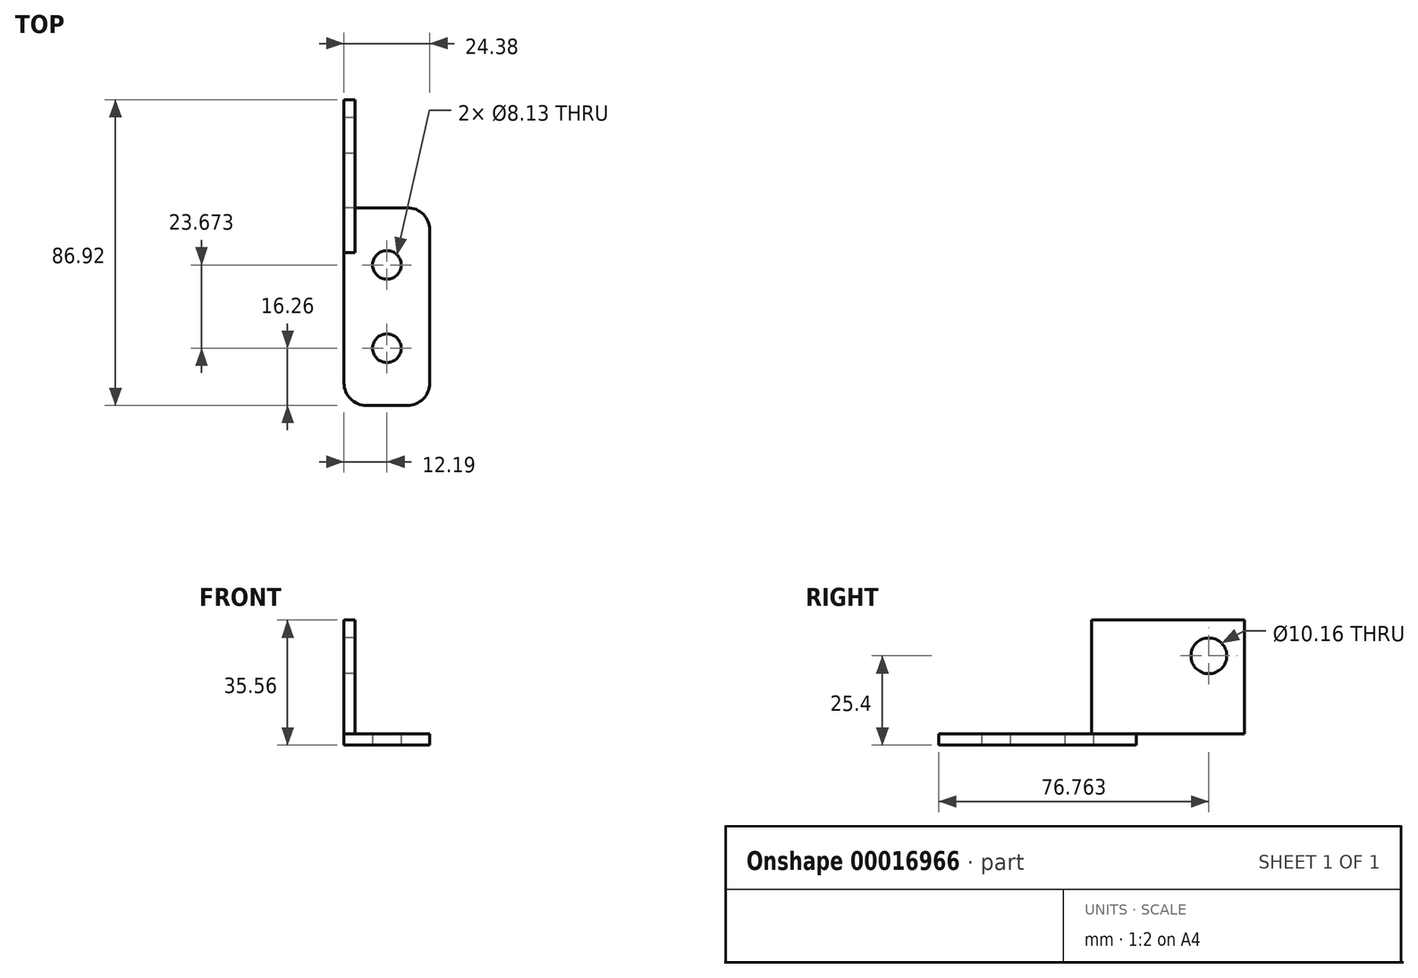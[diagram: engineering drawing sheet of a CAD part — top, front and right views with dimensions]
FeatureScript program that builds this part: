
annotation { "Feature Type Name" : "Feature", "Feature Type Description" : "" }
export const myFeature = defineFeature(function(context is Context, id is Id, definition is map)
    precondition{}
    {
        {
            var Q0;
            Q0=qCreatedBy(makeId("Top.planeOp"),FACE);
            var sketch = newSketch(context, id + "F0", { "sketchPlane" : qUnion([Q0])});
            skCircle(sketch, "E0", {"center": v(0, 0) * mm, "radius": 4.06 * mm});
            skCircle(sketch, "E1", {"center": v(0, 23.67) * mm, "radius": 4.06 * mm});
            skLineSegment(sketch, "E2", {"start": v(0, 19.6) * mm, "end": v(0, 4.06) * mm, "construction": true});
            skLineSegment(sketch, "E3.rect.bottom", {"start": v(5.84, -16.26) * mm, "end": v(-5.84, -16.26) * mm});
            skLineSegment(sketch, "E3.rect.top", {"start": v(5.84, 39.93) * mm, "end": v(-12.2, 39.93) * mm});
            skLineSegment(sketch, "E3.rect.left", {"start": v(12.2, -9.9) * mm, "end": v(12.2, 33.58) * mm});
            skLineSegment(sketch, "E3.rect.right", {"start": v(-12.2, -9.9) * mm, "end": v(-12.2, 39.93) * mm});
            skPoint(sketch, "E3.rect.middle", {"position": v(0, 11.84) * mm});
            skLineSegment(sketch, "E4", {"start": v(0, 11.84) * mm, "end": v(12.2, 11.84) * mm, "construction": true});
            skLineSegment(sketch, "E5", {"start": v(0, 39.93) * mm, "end": v(0, 27.74) * mm, "construction": true});
            skPoint(sketch, "E6.visualSharp", {"position": v(12.2, -16.26) * mm});
            skArc(sketch, "E6.filletArc", {"start": v(5.84, -16.26) * mm, "mid": v(10.33, -14.4) * mm, "end": v(12.2, -9.9) * mm});
            skPoint(sketch, "E7.visualSharp", {"position": v(-12.2, -16.26) * mm});
            skArc(sketch, "E7.filletArc", {"start": v(-12.2, -9.9) * mm, "mid": v(-10.33, -14.4) * mm, "end": v(-5.84, -16.26) * mm});
            skPoint(sketch, "E8.visualSharp", {"position": v(12.2, 39.93) * mm});
            skArc(sketch, "E8.filletArc", {"start": v(12.2, 33.58) * mm, "mid": v(10.33, 38.07) * mm, "end": v(5.84, 39.93) * mm});
            skSolve(sketch);
        }
        {
            var Q0;
            Q0=makeQuery(id+"F0.imprint","IMPRINT",FACE,{"disambiguationData":[TD([[makeQuery(id+"F0.imprint","IMPRINT",EDGE,{"derivedFrom":sQuery(id+"F0.wireOp",EDGE,"E0")}),-1.0]])]});
            extrude(context, id + "F1", {"entities" : qUnion([Q0]), "depth" : 3.17 * mm});
        }
        {
            var Q0;
            Q0=makeQuery(id+"F1.opExtrude","SWEPT_FACE",FACE,{"disambiguationData":[OSD([sQuery(id+"F0.wireOp",EDGE,"E3.rect.right")])]});
            var sketch = newSketch(context, id + "F2", { "sketchPlane" : qUnion([Q0])});
            skCircle(sketch, "E9", {"center": v(-60.5, 25.4) * mm, "radius": 5.08 * mm});
            skLineSegment(sketch, "E10", {"start": v(-23.67, 12.6) * mm, "end": v(-23.67, -8.77) * mm, "construction": true});
            skLineSegment(sketch, "E11.bottom", {"start": v(-27.23, 3.18) * mm, "end": v(-70.66, 3.18) * mm});
            skLineSegment(sketch, "E11.top", {"start": v(-27.23, 35.56) * mm, "end": v(-70.66, 35.56) * mm});
            skLineSegment(sketch, "E11.left", {"start": v(-27.23, 3.18) * mm, "end": v(-27.23, 35.56) * mm});
            skLineSegment(sketch, "E11.right", {"start": v(-70.66, 3.17) * mm, "end": v(-70.66, 35.56) * mm});
            skLineSegment(sketch, "E12", {"start": v(-60.5, 35.56) * mm, "end": v(-60.5, 25.4) * mm, "construction": true});
            skLineSegment(sketch, "E13", {"start": v(-60.5, 25.4) * mm, "end": v(-70.66, 25.4) * mm, "construction": true});
            skSolve(sketch);
        }
        {
            var Q0;
            Q0=makeQuery(id+"F2.imprint","IMPRINT",FACE,{"disambiguationData":[TD([[makeQuery(id+"F2.imprint","IMPRINT",EDGE,{"derivedFrom":sQuery(id+"F2.wireOp",EDGE,"E9")}),-1.0]])]});
            extrude(context, id + "F3", {"entities" : qUnion([Q0]), "oppositeDirection" : true, "depth" : 3.17 * mm});
        }
    });
